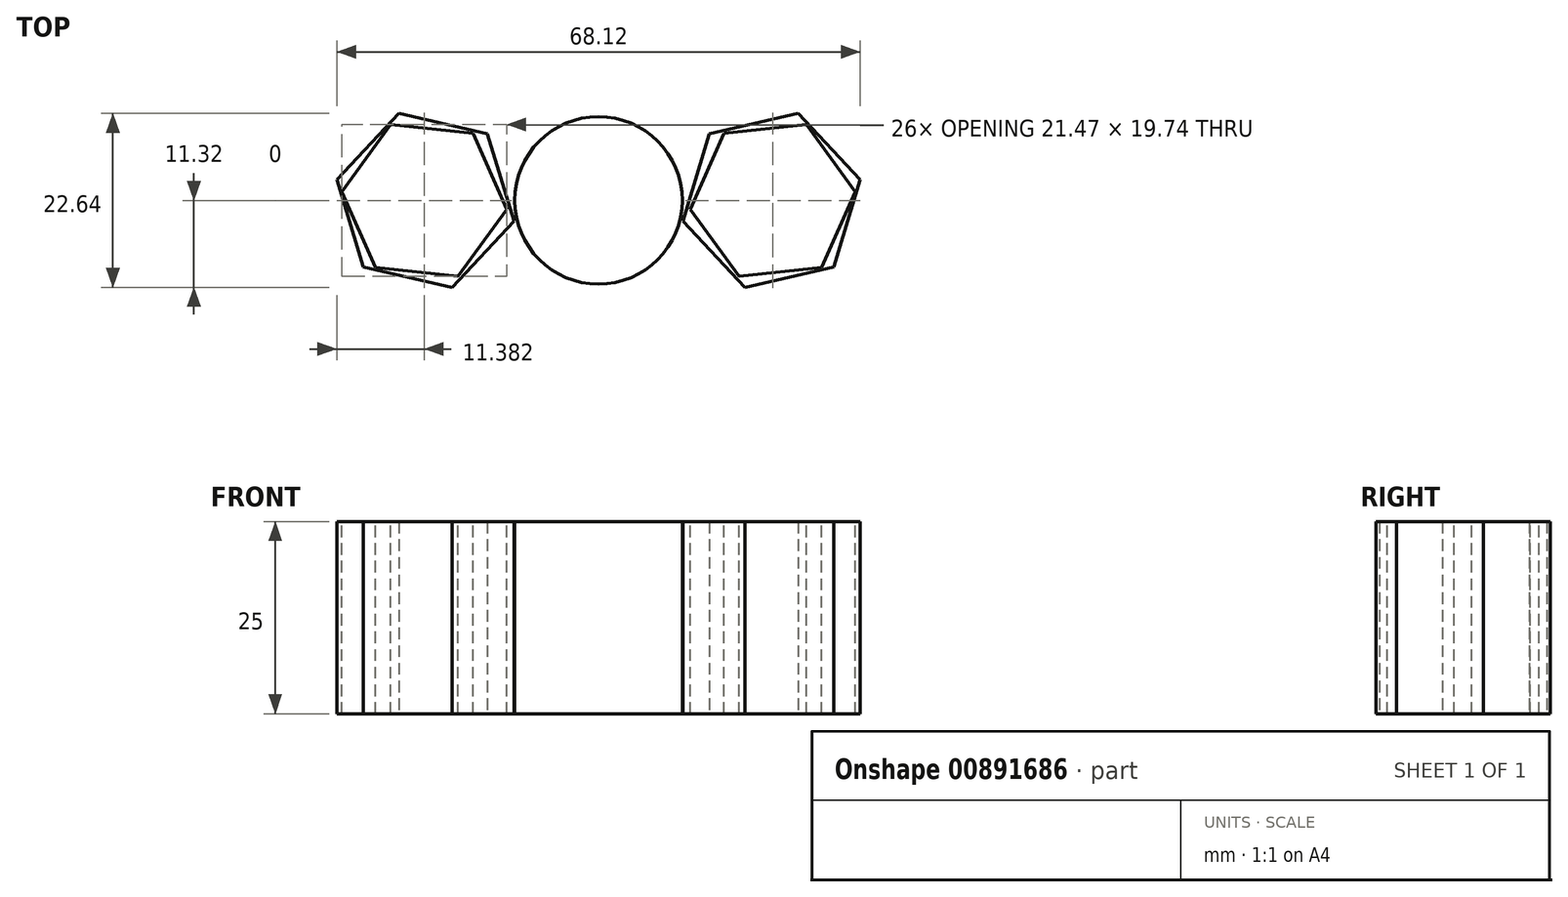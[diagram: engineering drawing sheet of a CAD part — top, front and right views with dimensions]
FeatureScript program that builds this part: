
annotation { "Feature Type Name" : "Feature", "Feature Type Description" : "" }
export const myFeature = defineFeature(function(context is Context, id is Id, definition is map)
    precondition{}
    {
        {
            var Q0;
            Q0=qCreatedBy(makeId("Top.planeOp"),FACE);
            var sketch = newSketch(context, id + "F0", { "sketchPlane" : qUnion([Q0])});
            skCircle(sketch, "E0", {"center": v(0, 0) * mm, "radius": 10.9 * mm});
            skCircle(sketch, "E1.cCircle", {"center": v(22.53, 0) * mm, "radius": 10.25 * mm, "construction": true});
            skLineSegment(sketch, "E1.0", {"start": v(30.6, -8.65) * mm, "end": v(19.07, -11.32) * mm});
            skLineSegment(sketch, "E1.1", {"start": v(19.07, -11.32) * mm, "end": v(11, -2.67) * mm});
            skLineSegment(sketch, "E1.2", {"start": v(11, -2.67) * mm, "end": v(14.45, 8.65) * mm});
            skLineSegment(sketch, "E1.3", {"start": v(14.45, 8.65) * mm, "end": v(25.98, 11.32) * mm});
            skLineSegment(sketch, "E1.4", {"start": v(25.98, 11.32) * mm, "end": v(34.06, 2.67) * mm});
            skLineSegment(sketch, "E1.5", {"start": v(34.06, 2.67) * mm, "end": v(30.6, -8.65) * mm});
            skPoint(sketch, "E1.0.midPoint", {"position": v(24.84, -9.99) * mm});
            skLineSegment(sketch, "E2.MirrorCS", {"start": v(-14.45, 8.65) * mm, "end": v(-25.98, 11.32) * mm});
            skLineSegment(sketch, "E3.MirrorCS", {"start": v(-11, -2.67) * mm, "end": v(-14.45, 8.65) * mm});
            skLineSegment(sketch, "E4.MirrorCS", {"start": v(-25.98, 11.32) * mm, "end": v(-34.06, 2.67) * mm});
            skLineSegment(sketch, "E5.MirrorCS", {"start": v(-34.06, 2.67) * mm, "end": v(-30.6, -8.65) * mm});
            skLineSegment(sketch, "E6.MirrorCS", {"start": v(-30.6, -8.65) * mm, "end": v(-19.07, -11.32) * mm});
            skLineSegment(sketch, "E7.MirrorCS", {"start": v(-19.07, -11.32) * mm, "end": v(-11, -2.67) * mm});
            skLineSegment(sketch, "E8", {"start": v(-14.45, 8.65) * mm, "end": v(-8.1, 7.3) * mm});
            skLineSegment(sketch, "E9", {"start": v(14.45, 8.65) * mm, "end": v(8.18, 7.2) * mm});
            skLineSegment(sketch, "E10", {"start": v(-19.07, -11.32) * mm, "end": v(-7.05, -8.31) * mm});
            skLineSegment(sketch, "E11", {"start": v(19.07, -11.32) * mm, "end": v(7.21, -8.17) * mm});
            skSolve(sketch);
        }
        {
            var Q0;
            Q0=makeQuery(id+"F0.imprint","IMPRINT",FACE,{"disambiguationData":[TD([[makeQuery(id+"F0.imprint","IMPRINT",EDGE,{"derivedFrom":sQuery(id+"F0.wireOp",EDGE,"E2.MirrorCS")}),1.0]])]});
            var Q1;
            Q1=makeQuery(id+"F0.imprint","IMPRINT",FACE,{"disambiguationData":[TD([[makeQuery(id+"F0.imprint","IMPRINT",EDGE,{"derivedFrom":sQuery(id+"F0.wireOp",EDGE,"E1.0")}),-1.0]])]});
            var Q2;
            {var subQ0=sQuery(id+"F0.wireOp",EDGE,"E0");var subQ1=makeQuery(id+"F0.imprint","INTERSECT",VERTEX,{"derivedFrom":[subQ0,sQuery(id+"F0.wireOp",EDGE,"E8")]});Q2=makeQuery(id+"F0.imprint","IMPRINT",FACE,{"disambiguationData":[TD([[makeQuery(id+"F0.imprint","IMPRINT",EDGE,{"disambiguationData":[TD([[subQ1,1.0]])],"derivedFrom":subQ0}),1.0]])]});}
            extrude(context, id + "F1", {"entities" : qUnion([Q0, Q1, Q2]), "depth" : 25 * mm, "offsetDistance" : 25 * mm});
        }
        {
            var Q0;
            Q0=makeQuery(id+"F1.opExtrude","CAP_FACE",FACE,{"disambiguationData":[OSD([sQuery(id+"F0.wireOp",EDGE,"E0"),sQuery(id+"F0.wireOp",EDGE,"E1.0"),sQuery(id+"F0.wireOp",EDGE,"E1.1"),sQuery(id+"F0.wireOp",EDGE,"E1.2"),sQuery(id+"F0.wireOp",EDGE,"E1.3"),sQuery(id+"F0.wireOp",EDGE,"E1.4"),sQuery(id+"F0.wireOp",EDGE,"E1.5"),sQuery(id+"F0.wireOp",EDGE,"E2.MirrorCS"),sQuery(id+"F0.wireOp",EDGE,"E3.MirrorCS"),sQuery(id+"F0.wireOp",EDGE,"E4.MirrorCS"),sQuery(id+"F0.wireOp",EDGE,"E5.MirrorCS"),sQuery(id+"F0.wireOp",EDGE,"E6.MirrorCS"),sQuery(id+"F0.wireOp",EDGE,"E7.MirrorCS")])],"isStart":false});
            var sketch = newSketch(context, id + "F2", { "sketchPlane" : qUnion([Q0])});
            skCircle(sketch, "E12.cCircle", {"center": v(-22.68, 0) * mm, "radius": 9.35 * mm, "construction": true});
            skLineSegment(sketch, "E12.0", {"start": v(-27.05, 9.87) * mm, "end": v(-16.32, 8.73) * mm});
            skLineSegment(sketch, "E12.1", {"start": v(-16.32, 8.73) * mm, "end": v(-11.94, -1.14) * mm});
            skLineSegment(sketch, "E12.2", {"start": v(-11.94, -1.14) * mm, "end": v(-18.3, -9.87) * mm});
            skLineSegment(sketch, "E12.3", {"start": v(-18.3, -9.87) * mm, "end": v(-29.04, -8.73) * mm});
            skLineSegment(sketch, "E12.4", {"start": v(-29.04, -8.73) * mm, "end": v(-33.41, 1.14) * mm});
            skLineSegment(sketch, "E12.5", {"start": v(-33.41, 1.14) * mm, "end": v(-27.05, 9.87) * mm});
            skPoint(sketch, "E12.0.midPoint", {"position": v(-21.69, 9.3) * mm});
            skLineSegment(sketch, "E13.MirrorCS", {"start": v(27.05, 9.87) * mm, "end": v(16.32, 8.73) * mm});
            skLineSegment(sketch, "E14.MirrorCS", {"start": v(16.32, 8.73) * mm, "end": v(11.94, -1.14) * mm});
            skLineSegment(sketch, "E15.MirrorCS", {"start": v(11.94, -1.14) * mm, "end": v(18.3, -9.87) * mm});
            skLineSegment(sketch, "E16.MirrorCS", {"start": v(18.3, -9.87) * mm, "end": v(29.04, -8.73) * mm});
            skLineSegment(sketch, "E17.MirrorCS", {"start": v(29.04, -8.73) * mm, "end": v(33.41, 1.14) * mm});
            skLineSegment(sketch, "E18.MirrorCS", {"start": v(33.41, 1.14) * mm, "end": v(27.05, 9.87) * mm});
            skSolve(sketch);
        }
        {
            var Q0;
            Q0 = qSketchRegion(id + "F2", true);
            extrude(context, id + "F3", {"entities" : qUnion([Q0]), "operationType" : NewBodyOperationType.REMOVE, "oppositeDirection" : true, "depth" : 25 * mm, "offsetDistance" : 25 * mm});
        }
    });
